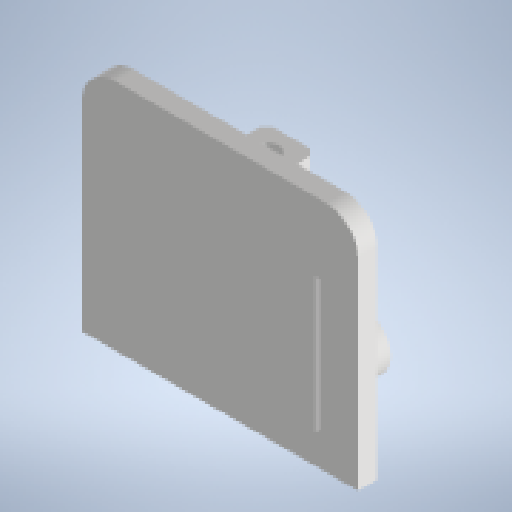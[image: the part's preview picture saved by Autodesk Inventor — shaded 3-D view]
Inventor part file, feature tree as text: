
AUTODESK INVENTOR PART (.ipt)
format: ipt  version: 2023 (Build 270158000, 158)  size: 321,024 bytes
history: native  units: mm
features: extrude x7, sketch x7, other x2, pattern_linear x2, chamfer x2, projected_geometry x2, fillet x1
ambient origin geometry x8: Origin, YZ Plane, XZ Plane, XY Plane, X Axis, Y Axis, Z Axis, Center Point
bodies: Body1 (feature_tree)
feature tree (23):
  other  "솔리드1"
  extrude  "돌출1"  Depth=42.5mm
  fillet  "모깎기1"  Radius=36.25mm
  other  "작업 평면1"
  extrude  "돌출2"  Depth=3.0mm TaperAngle=0.0deg
  pattern_linear  "직사각형 패턴1"  Spacing1=5.0mm  [1 undecoded]
  extrude  "돌출3"  [1 undecoded]
  extrude  "돌출4"  Depth=4.0mm
  extrude  "돌출5"  Depth=4.0mm
  chamfer  "모따기1"  Distance=8.0mm
  extrude  "돌출6"  Depth=10.0mm
  extrude  "돌출9"  Depth=2.0mm TaperAngle=0.0deg
  chamfer  "모따기3"  Distance=22.5mm
  pattern_linear  "직사각형 패턴2"  Spacing1=15.8mm  [1 undecoded]
  sketch  "스케치1"
  sketch  "스케치2"
  sketch  "스케치3"
  sketch  "스케치4"
  sketch  "스케치5"
  sketch  "스케치6"
  projected_geometry  "투영된 루프1"
  projected_geometry  "투영된 루프2"
  sketch  "스케치9"
note: 3 required parameter values undecoded (feature->parameter linkage not recoverable at this tier; creation-order binding heuristic only, values carry confidence <= 0.55)
